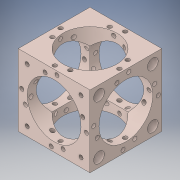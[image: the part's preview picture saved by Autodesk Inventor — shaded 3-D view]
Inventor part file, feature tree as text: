
AUTODESK INVENTOR PART (.ipt)
format: ipt  version: 2016 (Build 200138000, 138)  size: 574,976 bytes
history: native  units: mm
features: thread x56, other x2
ambient origin geometry x8: Origin, YZ Plane, XZ Plane, XY Plane, X Axis, Y Axis, Z Axis, Center Point
bodies: Solid1 (feature_tree)
feature tree (58):
  other  "Cube_30.iam"
  other  "00012269.ipt:1"
  thread  "GEWINDEHUELSE.ipt:1"  [1 undecoded]
  thread  "GEWINDEHUELSE_1.ipt:1"  [1 undecoded]
  thread  "GEWINDEHUELSE_2.ipt:1"  [1 undecoded]
  thread  "GEWINDEHUELSE_3.ipt:1"  [1 undecoded]
  thread  "GEWINDEHUELSE_4.ipt:1"  [1 undecoded]
  thread  "GEWINDEHUELSE_5.ipt:1"  [1 undecoded]
  thread  "GEWINDEHUELSE_6.ipt:1"  [1 undecoded]
  thread  "GEWINDEHUELSE_7.ipt:1"  [1 undecoded]
  thread  "GEWINDEHUELSE_8.ipt:1"  [1 undecoded]
  thread  "GEWINDEHUELSE_9.ipt:1"  [1 undecoded]
  thread  "GEWINDEHUELSE_10.ipt:1"  [1 undecoded]
  thread  "GEWINDEHUELSE_11.ipt:1"  [1 undecoded]
  thread  "GEWINDEHUELSE_12.ipt:1"  [1 undecoded]
  thread  "GEWINDEHUELSE_13.ipt:1"  [1 undecoded]
  thread  "GEWINDEHUELSE_14.ipt:1"  [1 undecoded]
  thread  "GEWINDEHUELSE_15.ipt:1"  [1 undecoded]
  thread  "GEWINDEHUELSE_16.ipt:1"  [1 undecoded]
  thread  "GEWINDEHUELSE_17.ipt:1"  [1 undecoded]
  thread  "GEWINDEHUELSE_18.ipt:1"  [1 undecoded]
  thread  "GEWINDEHUELSE_19.ipt:1"  [1 undecoded]
  thread  "GEWINDEHUELSE_20.ipt:1"  [1 undecoded]
  thread  "GEWINDEHUELSE_21.ipt:1"  [1 undecoded]
  thread  "GEWINDEHUELSE_22.ipt:1"  [1 undecoded]
  thread  "GEWINDEHUELSE_23.ipt:1"  [1 undecoded]
  thread  "GEWINDEHUELSE_24.ipt:1"  [1 undecoded]
  thread  "GEWINDEHUELSE_25.ipt:1"  [1 undecoded]
  thread  "GEWINDEHUELSE_26.ipt:1"  [1 undecoded]
  thread  "GEWINDEHUELSE_27.ipt:1"  [1 undecoded]
  thread  "GEWINDEHUELSE_28.ipt:1"  [1 undecoded]
  thread  "GEWINDEHUELSE_29.ipt:1"  [1 undecoded]
  thread  "GEWINDEHUELSE_30.ipt:1"  [1 undecoded]
  thread  "GEWINDEHUELSE_31.ipt:1"  [1 undecoded]
  thread  "GEWINDEHUELSE_32.ipt:1"  [1 undecoded]
  thread  "GEWINDEHUELSE_33.ipt:1"  [1 undecoded]
  thread  "GEWINDEHUELSE_34.ipt:1"  [1 undecoded]
  thread  "GEWINDEHUELSE_35.ipt:1"  [1 undecoded]
  thread  "GEWINDEHUELSE_36.ipt:1"  [1 undecoded]
  thread  "GEWINDEHUELSE_37.ipt:1"  [1 undecoded]
  thread  "GEWINDEHUELSE_38.ipt:1"  [1 undecoded]
  thread  "GEWINDEHUELSE_39.ipt:1"  [1 undecoded]
  thread  "GEWINDEHUELSE_40.ipt:1"  [1 undecoded]
  thread  "GEWINDEHUELSE_41.ipt:1"  [1 undecoded]
  thread  "GEWINDEHUELSE_42.ipt:1"  [1 undecoded]
  thread  "GEWINDEHUELSE_43.ipt:1"  [1 undecoded]
  thread  "GEWINDEHUELSE_44.ipt:1"  [1 undecoded]
  thread  "GEWINDEHUELSE_45.ipt:1"  [1 undecoded]
  thread  "GEWINDEHUELSE_46.ipt:1"  [1 undecoded]
  thread  "GEWINDEHUELSE_47.ipt:1"  [1 undecoded]
  thread  "GEWINDEHUELSE_48.ipt:1"  [1 undecoded]
  thread  "GEWINDEHUELSE_49.ipt:1"  [1 undecoded]
  thread  "GEWINDEHUELSE_50.ipt:1"  [1 undecoded]
  thread  "GEWINDEHUELSE_51.ipt:1"  [1 undecoded]
  thread  "GEWINDEHUELSE_52.ipt:1"  [1 undecoded]
  thread  "GEWINDEHUELSE_53.ipt:1"  [1 undecoded]
  thread  "GEWINDEHUELSE_54.ipt:1"  [1 undecoded]
  thread  "GEWINDEHUELSE_55.ipt:1"  [1 undecoded]
note: 56 required parameter values undecoded (feature->parameter linkage not recoverable at this tier; creation-order binding heuristic only, values carry confidence <= 0.55)
